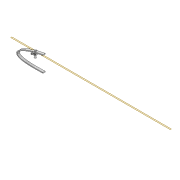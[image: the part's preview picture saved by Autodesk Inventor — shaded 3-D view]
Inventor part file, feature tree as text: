
AUTODESK INVENTOR PART (.ipt)
format: ipt  version: 2022 (Build 260153000, 153)  size: 554,496 bytes
history: native  units: mm
features: extrude x10, sketch x10, projected_geometry x7, plane x4, shell x1, fillet x1
ambient origin geometry x8: Origin, YZ Plane, XZ Plane, XY Plane, X Axis, Y Axis, Z Axis, Center Point
bodies: Solid1 (feature_tree)
feature tree (33):
  extrude  "Extrusion1"  Depth=3.0mm
  shell  "Shell1"  Thickness=5.215mm
  plane  "Work Plane3"
  sketch  "Sketch26"  dims[d69=4.1mm d70=63.6mm]
  plane  "Work Plane4"
  extrude  "Extrusion9"  Depth=63.6mm
  plane  "Work Plane5"
  extrude  "Extrusion10"  Depth=4.2mm
  extrude  "Extrusion11"  Depth=6.0mm
  extrude  "Extrusion12"  Depth=21.0mm TaperAngle=0.0deg
  plane  "Work Plane6"
  extrude  "Extrusion13"  Depth=5.0mm
  extrude  "Extrusion15"  Depth=3.0mm TaperAngle=0.0deg
  extrude  "Extrusion16"  Depth=2.0mm
  extrude  "Extrusion17"  Depth=4.0mm
  fillet  "Fillet2"  Radius=4.0mm
  extrude  "Extrusion18"  Depth=95.0mm
  sketch  "Sketch3"  dims[d0=12.0mm d1=0.0mm d2=3.0mm d68=5.215mm]
  sketch  "Sketch27"  dims[d71=12.0mm d72=4.2mm]
  projected_geometry  "Projected Loop13"
  sketch  "Sketch29"  dims[d73=63.6mm d74=6.0mm]
  sketch  "Sketch30"  dims[d75=7.0mm d76=21.0mm d77=0.0mm]
  projected_geometry  "Projected Loop14"
  sketch  "Sketch31"  dims[d78=-11.5mm d79=5.0mm]
  projected_geometry  "Projected Loop15"
  projected_geometry  "Projected Loop16"
  projected_geometry  "Projected Loop17"
  sketch  "Sketch33"  dims[d80=10.0mm d83=3.0mm d84=0.0mm]
  sketch  "Sketch34"  dims[d86=0.65mm d87=2.0mm]
  projected_geometry  "Projected Loop18"
  sketch  "Sketch35"  dims[d88=2.0mm d89=4.0mm d90=4.0mm]
  projected_geometry  "Projected Loop19"
  sketch  "Sketch36"  dims[d91=3.0mm d92=0.0mm d93=12.0mm d94=7.0mm d95=0.0mm d96=28.0mm d98=9.0mm d99=0.0mm d103=200.0mm d104=100.0mm d105=0.0mm d106=7.0mm d107=4.1mm d108=7.0mm d109=2.0mm d110=0.0mm d111=2.0mm d112=0.0mm d113=2.0mm d114=95.0mm d115=10.0mm d116=0.0mm]
